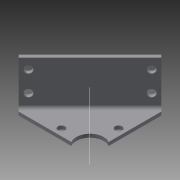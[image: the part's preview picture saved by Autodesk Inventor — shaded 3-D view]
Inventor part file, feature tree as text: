
AUTODESK INVENTOR PART (.ipt)
format: ipt  version: 2013 (Build 170138000, 138)  size: 139,776 bytes
history: native  units: in
note: dims shown in document units (in); Inventor stores cm internally (conversion verified against a paired STEP export)
features: sheet_metal_op x4, other x4, sketch x3
ambient origin geometry x8: Origin, YZ Plane, XZ Plane, XY Plane, X Axis, Y Axis, Z Axis, Center Point
bodies: Solid1 (feature_tree)
feature tree (11):
  sheet_metal_op  "Face1"
  sheet_metal_op  "Flange1"
  sketch  "Sketch3"  dims[d2=0.26in d3=0.26in d4=0.26in d5=1.0in d8=0.25in d9=0.0in d10=0.25in d11=0.25in d12=45.0deg d13=0.75in d14=0.125in d15=0.125in d16=0.0625in d17=0.25in d18=0.125in d19=1.75in d20=90.0deg d21=0.125in d22=0.5in d23=0.125in d24=0.125in d35=3.685in d36=0.266in d37=0.266in d38=0.266in d39=0.266in d40=0.25in d41=0.375in d42=0.375in d43=0.25in d44=0.375in d45=0.375in d47=0.25in d48=0.25in d49=0.125in d50=0.0in]
  other  "Work Axis1"
  sketch  "Sketch1"  dims[d0=2.09in]
  other  "Plate1"
  sketch  "Sketch2"  dims[d1=0.26in]
  other  "Plate2"
  sheet_metal_op  "Bend1"
  sheet_metal_op  "Corner1"
  other  "Cut3"
